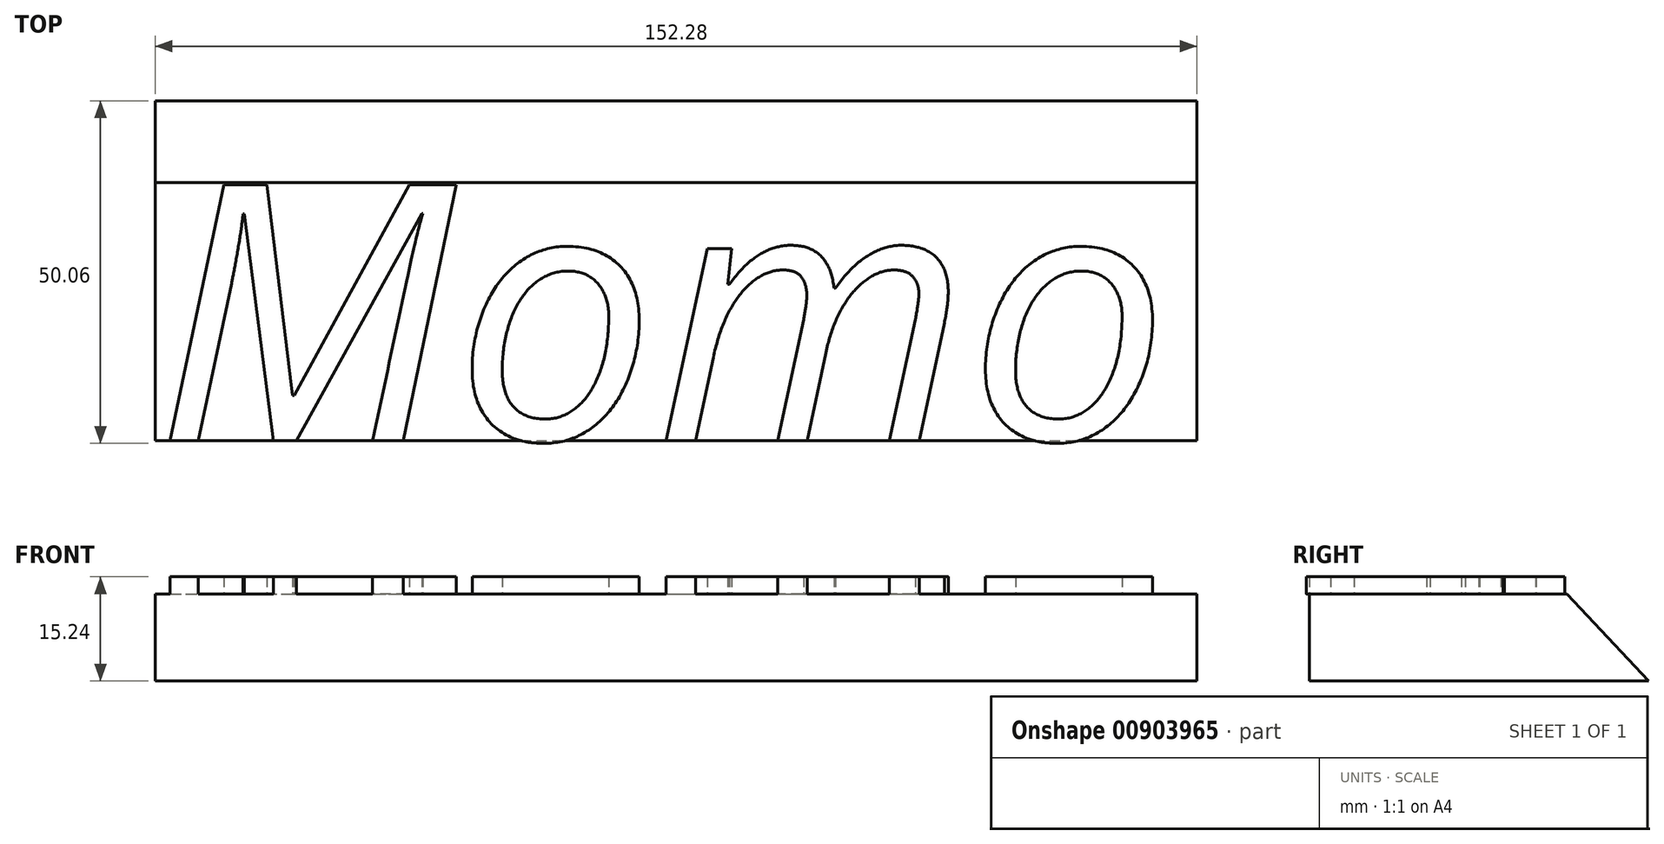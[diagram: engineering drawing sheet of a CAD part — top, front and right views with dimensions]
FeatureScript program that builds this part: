
annotation { "Feature Type Name" : "Feature", "Feature Type Description" : "" }
export const myFeature = defineFeature(function(context is Context, id is Id, definition is map)
    precondition{}
    {
        {
            var Q0;
            Q0=qCreatedBy(makeId("Top.planeOp"),FACE);
            var sketch = newSketch(context, id + "F0", { "sketchPlane" : qUnion([Q0])});
            skLineSegment(sketch, "E0.bottom", {"start": v(-76.82, 27.3) * mm, "end": v(75.46, 27.3) * mm});
            skLineSegment(sketch, "E0.top", {"start": v(-76.82, -22.36) * mm, "end": v(75.46, -22.36) * mm});
            skLineSegment(sketch, "E0.left", {"start": v(-76.82, 27.3) * mm, "end": v(-76.82, -22.36) * mm});
            skLineSegment(sketch, "E0.right", {"start": v(75.46, 27.3) * mm, "end": v(75.46, -22.36) * mm});
            skSolve(sketch);
        }
        {
            var Q0;
            Q0 = qSketchRegion(id + "F0", true);
            extrude(context, id + "F1", {"entities" : qUnion([Q0]), "depth" : 12.7 * mm, "offsetDistance" : 25.4 * mm});
        }
        {
            var Q0;
            Q0=makeQuery(id+"F1.opExtrude","SWEPT_FACE",FACE,{"disambiguationData":[OSD([sQuery(id+"F0.wireOp",EDGE,"E0.right")])]});
            var sketch = newSketch(context, id + "F2", { "sketchPlane" : qUnion([Q0])});
            skLineSegment(sketch, "E1", {"start": v(27.3, 0) * mm, "end": v(27.3, 12.7) * mm});
            skLineSegment(sketch, "E2", {"start": v(27.3, 12.7) * mm, "end": v(15.33, 12.7) * mm});
            skLineSegment(sketch, "E3", {"start": v(15.33, 12.7) * mm, "end": v(27.3, 0) * mm});
            skSolve(sketch);
        }
        {
            var Q0;
            Q0 = qSketchRegion(id + "F2", true);
            extrude(context, id + "F3", {"entities" : qUnion([Q0]), "operationType" : NewBodyOperationType.REMOVE, "oppositeDirection" : true, "depth" : 152.4 * mm, "offsetDistance" : 25.4 * mm});
        }
        {
            var Q0;
            Q0=makeQuery(id+"F1.opExtrude","CAP_FACE",FACE,{"disambiguationData":[OSD([sQuery(id+"F0.wireOp",EDGE,"E0.bottom"),sQuery(id+"F0.wireOp",EDGE,"E0.top"),sQuery(id+"F0.wireOp",EDGE,"E0.left"),sQuery(id+"F0.wireOp",EDGE,"E0.right")])],"isStart":false});
            var sketch = newSketch(context, id + "F4", { "sketchPlane" : qUnion([Q0])});
            skText(sketch, "E4", { "text": "Momo ", "fontName": "OpenSans-Italic.ttf"});
            const initialGuessF4  = {"E4": [-0.07682, -0.02236, 1, 0, 0.0377]};
            skSetInitialGuess(sketch, initialGuessF4);
            skSolve(sketch);
        }
        {
            var Q0;
            Q0 = qSketchRegion(id + "F4", true);
            extrude(context, id + "F5", {"entities" : qUnion([Q0]), "operationType" : NewBodyOperationType.ADD, "depth" : 2.54 * mm, "offsetDistance" : 25.4 * mm});
        }
    });
